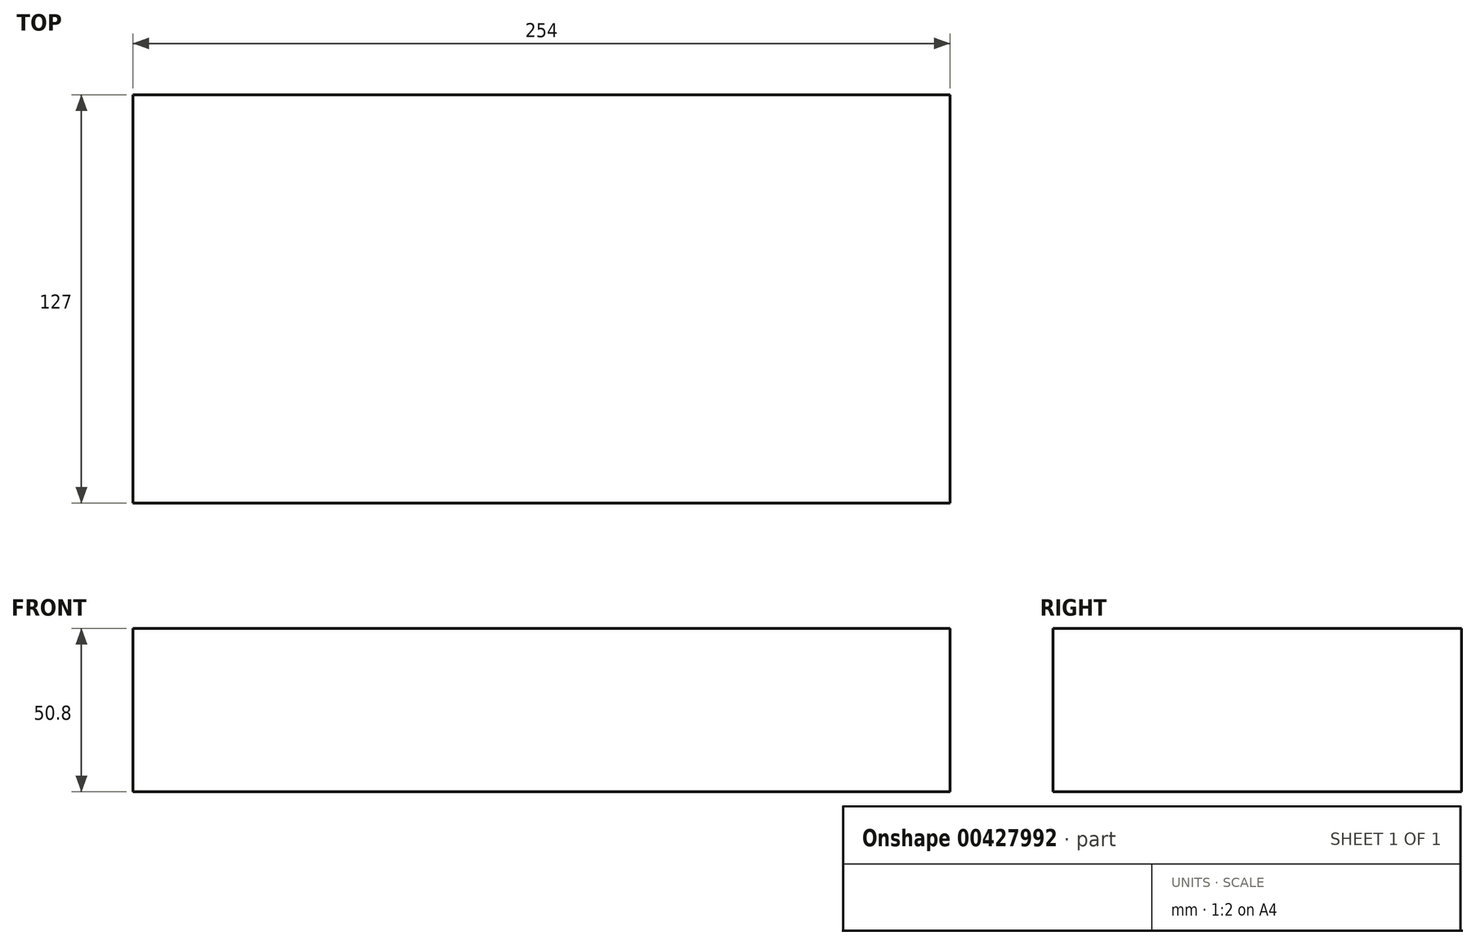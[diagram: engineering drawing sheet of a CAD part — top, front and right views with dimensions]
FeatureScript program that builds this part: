
annotation { "Feature Type Name" : "Feature", "Feature Type Description" : "" }
export const myFeature = defineFeature(function(context is Context, id is Id, definition is map)
    precondition{}
    {
        {
            var Q0;
            Q0=qCreatedBy(makeId("Top.planeOp"),FACE);
            var sketch = newSketch(context, id + "F0", { "sketchPlane" : qUnion([Q0])});
            skLineSegment(sketch, "E0.bottom", {"start": v(-141.39, 62.52) * mm, "end": v(112.61, 62.52) * mm});
            skLineSegment(sketch, "E0.top", {"start": v(-141.39, -64.48) * mm, "end": v(112.61, -64.48) * mm});
            skLineSegment(sketch, "E0.left", {"start": v(-141.39, 62.52) * mm, "end": v(-141.39, -64.48) * mm});
            skLineSegment(sketch, "E0.right", {"start": v(112.61, 62.52) * mm, "end": v(112.61, -64.48) * mm});
            skSolve(sketch);
        }
        {
            var Q0;
            Q0 = qSketchRegion(id + "F0", true);
            extrude(context, id + "F1", {"entities" : qUnion([Q0]), "depth" : 50.8 * mm});
        }
    });
